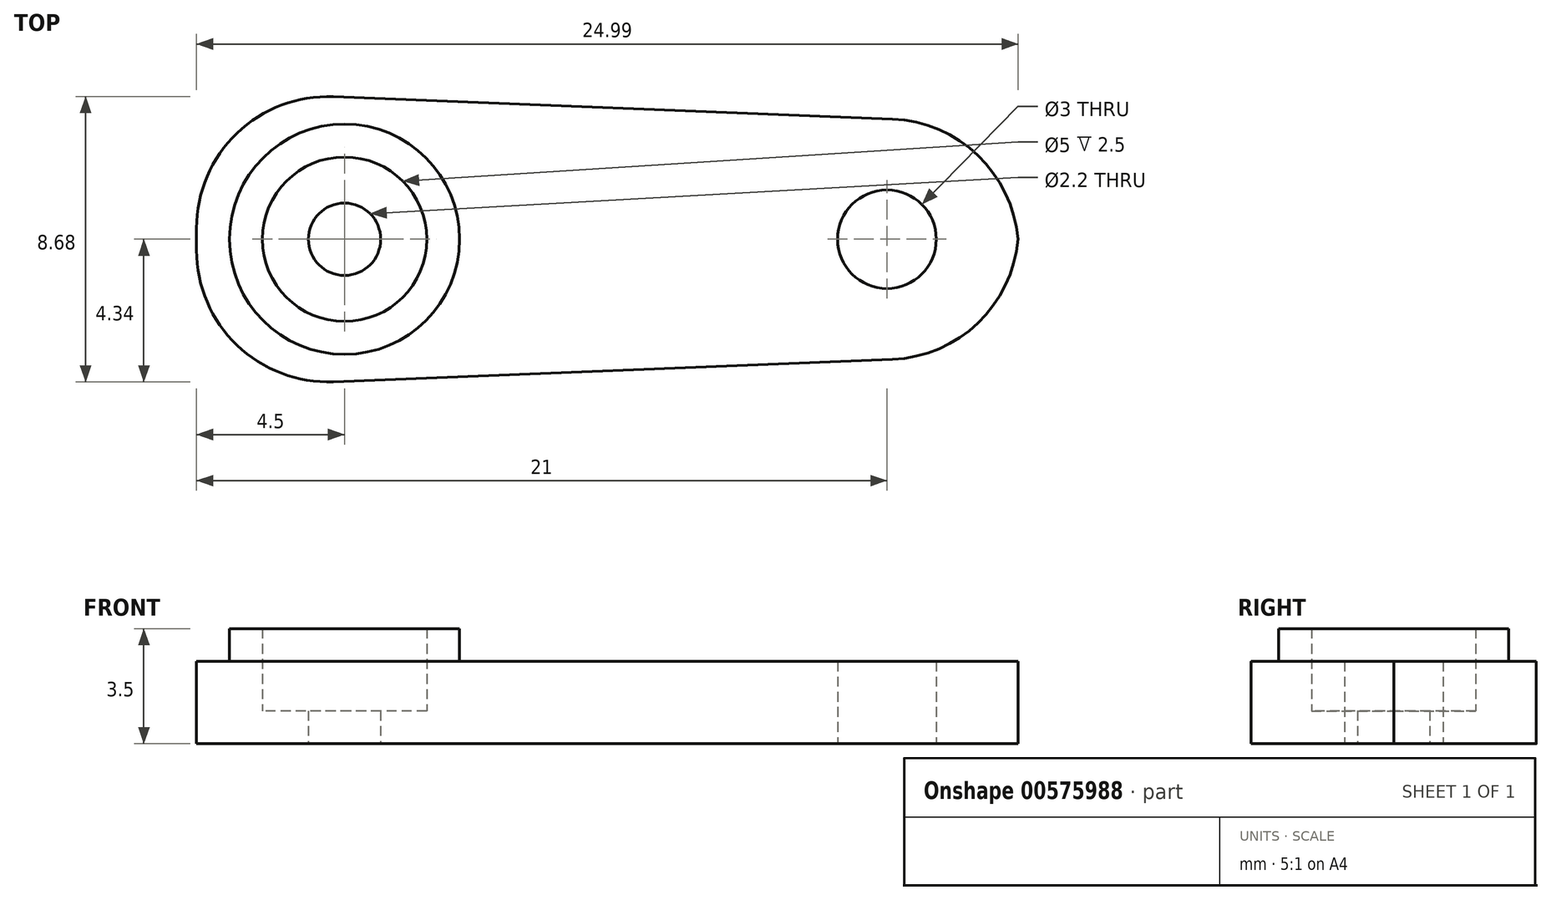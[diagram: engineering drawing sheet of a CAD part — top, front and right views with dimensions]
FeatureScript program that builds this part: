
annotation { "Feature Type Name" : "Feature", "Feature Type Description" : "" }
export const myFeature = defineFeature(function(context is Context, id is Id, definition is map)
    precondition{}
    {
        {
            var Q0;
            Q0=qCreatedBy(makeId("Top.planeOp"),FACE);
            var sketch = newSketch(context, id + "F0", { "sketchPlane" : qUnion([Q0])});
            skLineSegment(sketch, "E0.left", {"start": v(0, -11) * mm, "end": v(0, -20) * mm});
            skLineSegment(sketch, "E0.right", {"start": v(25, -12) * mm, "end": v(25, -19) * mm});
            skCircle(sketch, "E1", {"center": v(21, -15.5) * mm, "radius": 1.5 * mm});
            skCircle(sketch, "E2", {"center": v(4.5, -15.5) * mm, "radius": 2.5 * mm});
            skLineSegment(sketch, "E3", {"start": v(0, -11) * mm, "end": v(25, -12) * mm});
            skLineSegment(sketch, "E4", {"start": v(0, -20) * mm, "end": v(25, -19) * mm});
            skLineSegment(sketch, "E5", {"start": v(0, -11) * mm, "end": v(26.7, -11) * mm, "construction": true});
            skSolve(sketch);
        }
        {
            var Q0;
            Q0 = qSketchRegion(id + "F0", true);
            extrude(context, id + "F1", {"entities" : qUnion([Q0]), "depth" : 2.5 * mm, "offsetDistance" : 25 * mm});
        }
        {
            var Q0;
            Q0=makeQuery(id+"F1.opExtrude","SWEPT_EDGE",EDGE,{"disambiguationData":[OSD([sQuery(id+"F0.wireOp",EDGE,"E0.top"),sQuery(id+"F0.wireOp",EDGE,"E0.right")])]});
            var Q1;
            Q1=makeQuery(id+"F1.opExtrude","SWEPT_EDGE",EDGE,{"disambiguationData":[OSD([sQuery(id+"F0.wireOp",EDGE,"E0.bottom"),sQuery(id+"F0.wireOp",EDGE,"E0.right")])]});
            var Q2;
            Q2=makeQuery(id+"F1.opExtrude","SWEPT_EDGE",EDGE,{"disambiguationData":[OSD([sQuery(id+"F0.wireOp",EDGE,"E0.top"),sQuery(id+"F0.wireOp",EDGE,"E0.left")])]});
            var Q3;
            Q3=makeQuery(id+"F1.opExtrude","SWEPT_EDGE",EDGE,{"disambiguationData":[OSD([sQuery(id+"F0.wireOp",EDGE,"E0.bottom"),sQuery(id+"F0.wireOp",EDGE,"E0.left")])]});
            fillet(context, id + "F2", {"entities" : qUnion([Q0, Q1, Q2, Q3]), "radius" : 4 * mm, "tangentPropagation" : true, "allowEdgeOverflow" : false});
        }
        {
            var Q0;
            Q0=makeQuery(id+"F1.opExtrude","CAP_FACE",FACE,{"disambiguationData":[OSD([sQuery(id+"F0.wireOp",EDGE,"E0.left"),sQuery(id+"F0.wireOp",EDGE,"E0.right"),sQuery(id+"F0.wireOp",EDGE,"E1"),sQuery(id+"F0.wireOp",EDGE,"E2"),sQuery(id+"F0.wireOp",EDGE,"E3"),sQuery(id+"F0.wireOp",EDGE,"E4")])],"isStart":false});
            var sketch = newSketch(context, id + "F3", { "sketchPlane" : qUnion([Q0])});
            skCircle(sketch, "E6", {"center": v(4.5, -15.5) * mm, "radius": 3.5 * mm});
            skCircle(sketch, "E7.0", {"center": v(4.5, -15.5) * mm, "radius": 2.5 * mm});
            skSolve(sketch);
        }
        {
            var Q0;
            Q0 = qSketchRegion(id + "F3", true);
            extrude(context, id + "F4", {"entities" : qUnion([Q0]), "operationType" : NewBodyOperationType.ADD, "depth" : 1 * mm, "offsetDistance" : 25 * mm});
        }
        {
            var Q0;
            Q0=qCreatedBy(makeId("Top.planeOp"),FACE);
            var sketch = newSketch(context, id + "F5", { "sketchPlane" : qUnion([Q0])});
            skCircle(sketch, "E8.0", {"center": v(4.5, -15.5) * mm, "radius": 2.5 * mm});
            skCircle(sketch, "E9", {"center": v(4.5, -15.5) * mm, "radius": 1.1 * mm});
            skSolve(sketch);
        }
        {
            var Q0;
            Q0=makeQuery(id+"F5.imprint","IMPRINT",FACE,{"disambiguationData":[TD([[makeQuery(id+"F5.imprint","IMPRINT",EDGE,{"derivedFrom":sQuery(id+"F5.wireOp",EDGE,"E8.0")}),1.0]])]});
            extrude(context, id + "F6", {"entities" : qUnion([Q0]), "operationType" : NewBodyOperationType.ADD, "depth" : 1 * mm, "offsetDistance" : 25 * mm});
        }
    });
